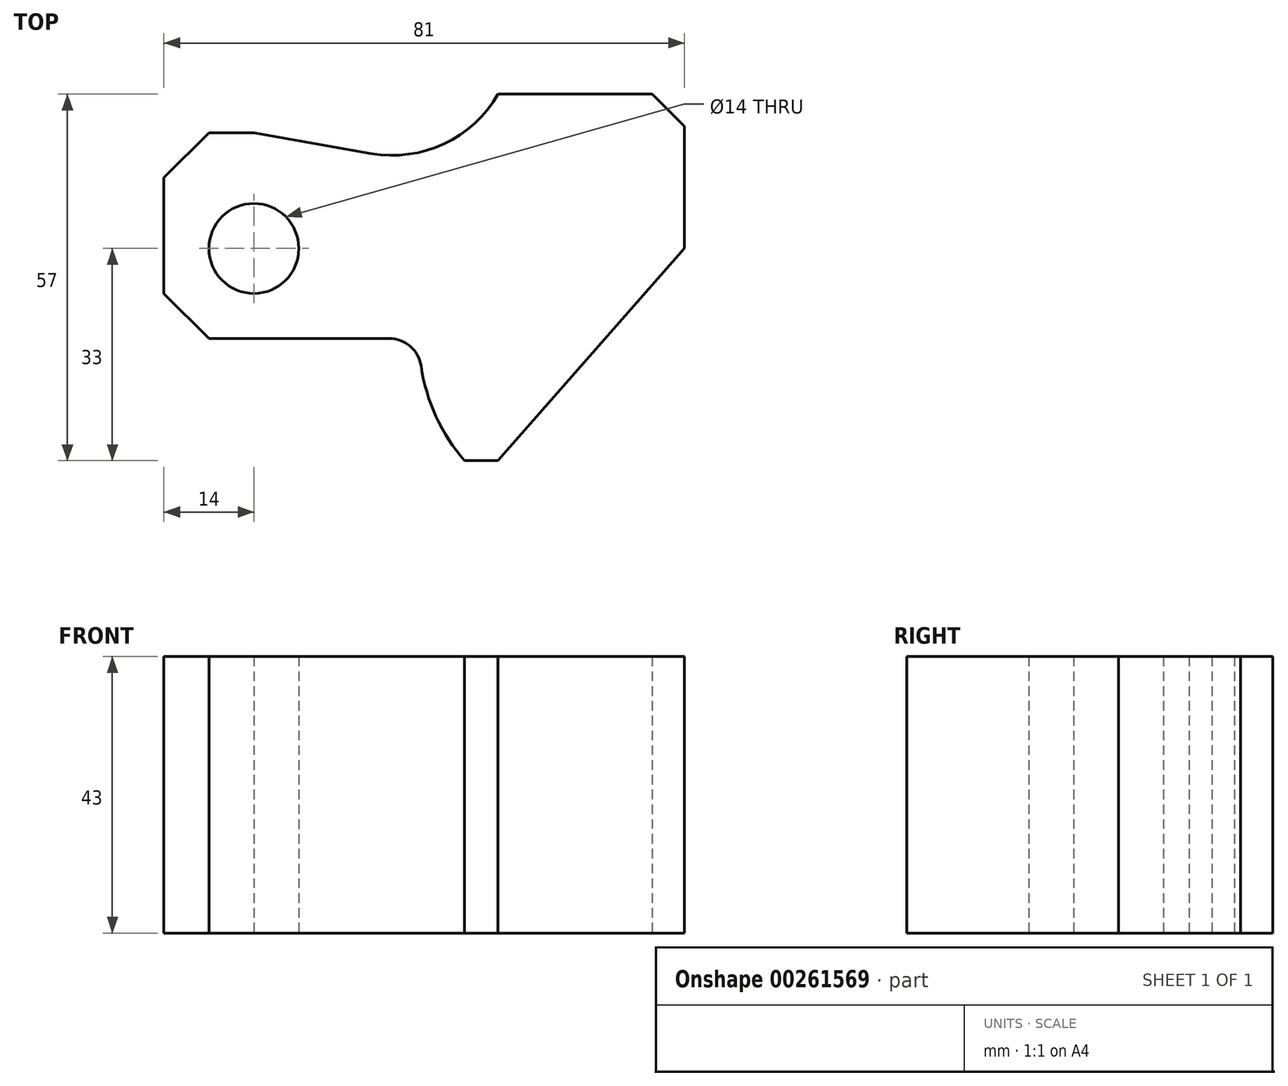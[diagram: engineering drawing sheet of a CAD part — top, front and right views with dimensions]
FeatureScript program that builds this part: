
annotation { "Feature Type Name" : "Feature", "Feature Type Description" : "" }
export const myFeature = defineFeature(function(context is Context, id is Id, definition is map)
    precondition{}
    {
        {
            var Q0;
            Q0=qCreatedBy(makeId("Top.planeOp"),FACE);
            var sketch = newSketch(context, id + "F0", { "sketchPlane" : qUnion([Q0])});
            skCircle(sketch, "E0", {"center": v(0, 0) * mm, "radius": 7 * mm});
            skLineSegment(sketch, "E1", {"start": v(-14, 11) * mm, "end": v(-14, -7) * mm});
            skLineSegment(sketch, "E2", {"start": v(-14, 11) * mm, "end": v(-7, 18) * mm});
            skLineSegment(sketch, "E3", {"start": v(-14, -7) * mm, "end": v(-7, -14) * mm});
            skLineSegment(sketch, "E4", {"start": v(-7, -14) * mm, "end": v(21.07, -14) * mm});
            skArc(sketch, "E5", {"start": v(26.01, -18.26) * mm, "mid": v(24.33, -15.21) * mm, "end": v(21.07, -14) * mm});
            skLineSegment(sketch, "E6", {"start": v(38, 24) * mm, "end": v(62, 24) * mm});
            skLineSegment(sketch, "E7", {"start": v(62, 24) * mm, "end": v(67, 19) * mm});
            skLineSegment(sketch, "E8", {"start": v(67, 19) * mm, "end": v(67, 0) * mm});
            skLineSegment(sketch, "E9", {"start": v(-7, 18) * mm, "end": v(0, 18) * mm});
            skLineSegment(sketch, "E10", {"start": v(0, 18) * mm, "end": v(18.24, 14.78) * mm});
            skArc(sketch, "E11", {"start": v(18.24, 14.78) * mm, "mid": v(29.57, 16.28) * mm, "end": v(38, 24) * mm});
            skLineSegment(sketch, "E12", {"start": v(26.01, -18.26) * mm, "end": v(26.01, -18.26) * mm});
            skArc(sketch, "E13", {"start": v(26.01, -18.26) * mm, "mid": v(28.35, -26.12) * mm, "end": v(32.79, -33) * mm});
            skLineSegment(sketch, "E14", {"start": v(67, 0) * mm, "end": v(38, -33) * mm});
            skLineSegment(sketch, "E15", {"start": v(38, -33) * mm, "end": v(32.79, -33) * mm});
            skLineSegment(sketch, "E16", {"start": v(-7, 18) * mm, "end": v(-20.41, 18) * mm, "construction": true});
            skLineSegment(sketch, "E17", {"start": v(-7, -14) * mm, "end": v(-20.57, -14) * mm, "construction": true});
            skLineSegment(sketch, "E18", {"start": v(0, 18) * mm, "end": v(11.72, 18) * mm, "construction": true});
            skSolve(sketch);
        }
        {
            var Q0;
            Q0=makeQuery(id+"F0.imprint","IMPRINT",FACE,{"disambiguationData":[TD([[makeQuery(id+"F0.imprint","IMPRINT",EDGE,{"derivedFrom":sQuery(id+"F0.wireOp",EDGE,"E0")}),-1.0]])]});
            extrude(context, id + "F1", {"entities" : qUnion([Q0]), "depth" : 43 * mm, "symmetric" : true});
        }
    });
